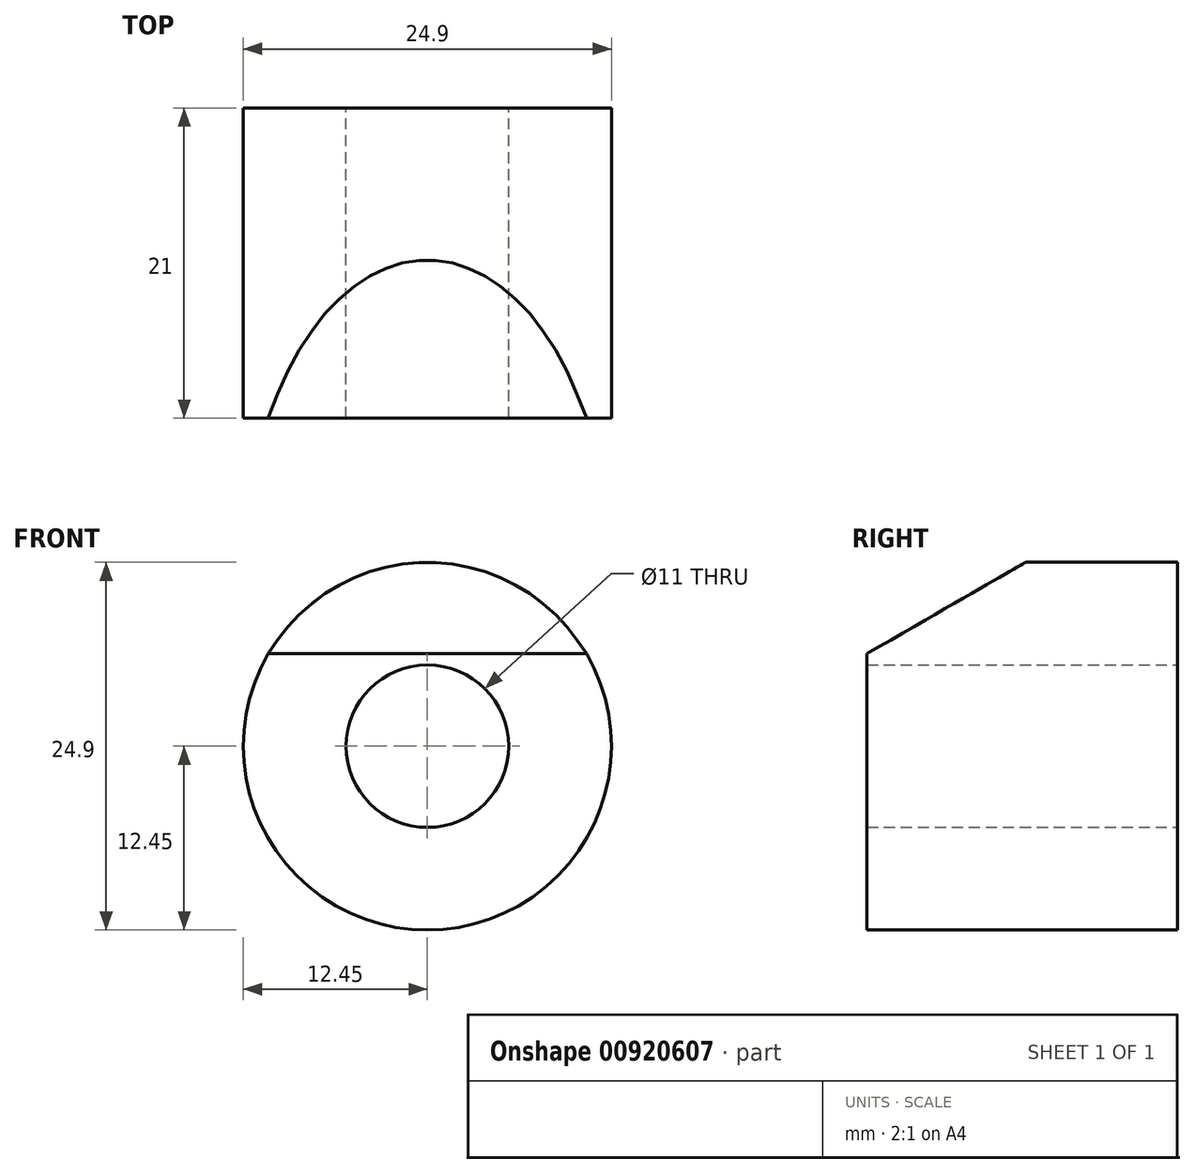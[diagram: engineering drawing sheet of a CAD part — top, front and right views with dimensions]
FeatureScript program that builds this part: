
annotation { "Feature Type Name" : "Feature", "Feature Type Description" : "" }
export const myFeature = defineFeature(function(context is Context, id is Id, definition is map)
    precondition{}
    {
        {
            var Q0;
            Q0=qCreatedBy(makeId("Front.planeOp"),FACE);
            var sketch = newSketch(context, id + "F0", { "sketchPlane" : qUnion([Q0])});
            skCircle(sketch, "E0", {"center": v(0, 0) * mm, "radius": 5.5 * mm});
            skCircle(sketch, "E1", {"center": v(0, 0) * mm, "radius": 12.45 * mm});
            skSolve(sketch);
        }
        {
            var Q0;
            Q0=makeQuery(id+"F0.imprint","IMPRINT",FACE,{"disambiguationData":[TD([[makeQuery(id+"F0.imprint","IMPRINT",EDGE,{"derivedFrom":sQuery(id+"F0.wireOp",EDGE,"E0")}),-1.0]])]});
            extrude(context, id + "F1", {"entities" : qUnion([Q0]), "depth" : 21 * mm, "offsetDistance" : 25 * mm});
        }
        {
            var Q0;
            Q0=qCreatedBy(makeId("Right.planeOp"),FACE);
            var sketch = newSketch(context, id + "F2", { "sketchPlane" : qUnion([Q0])});
            skLineSegment(sketch, "E2", {"start": v(0, -12.45) * mm, "end": v(-21.1, -12.45) * mm, "construction": true});
            skLineSegment(sketch, "E3", {"start": v(-21.1, 12.45) * mm, "end": v(-10.26, 12.45) * mm});
            skLineSegment(sketch, "E4.0", {"start": v(-21, 6.25) * mm, "end": v(-21, 12.45) * mm});
            skPoint(sketch, "E5.orphan", {"position": v(-21, -12.45) * mm});
            skLineSegment(sketch, "E6", {"start": v(-21, 6.25) * mm, "end": v(-10.26, 12.45) * mm});
            skSolve(sketch);
        }
        {
            var Q0;
            Q0=makeQuery(id+"F2.imprint","IMPRINT",FACE,{"disambiguationData":[TD([[makeQuery(id+"F2.imprint","IMPRINT",EDGE,{"derivedFrom":sQuery(id+"F2.wireOp",EDGE,"E3")}),-1.0]])]});
            extrude(context, id + "F3", {"entities" : qUnion([Q0]), "operationType" : NewBodyOperationType.REMOVE, "oppositeDirection" : true, "depth" : 25 * mm, "offsetDistance" : 25 * mm, "symmetric" : true});
        }
    });
